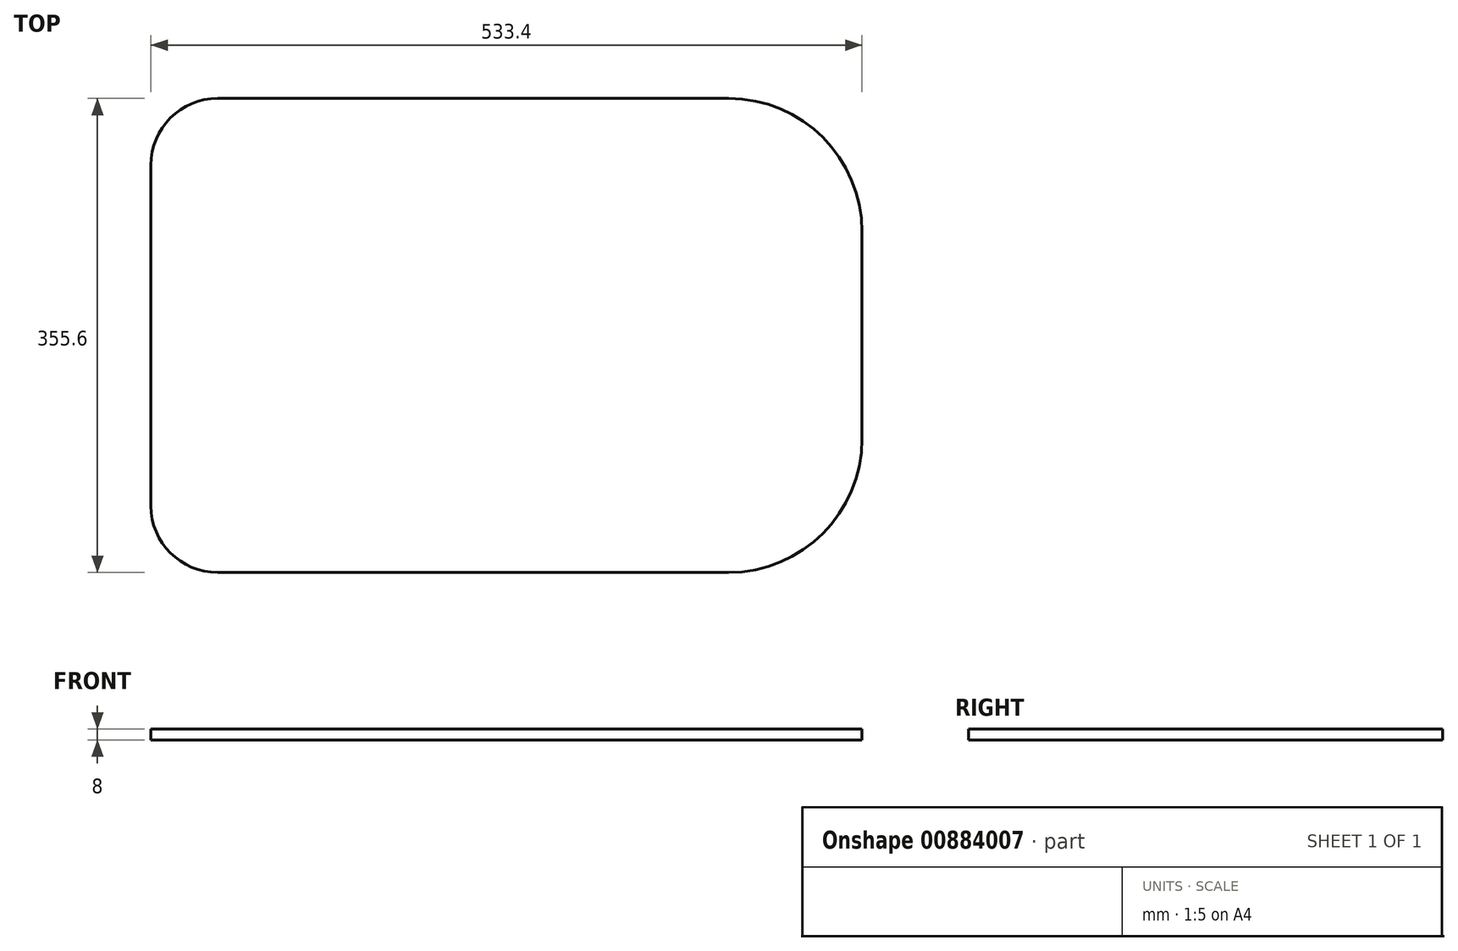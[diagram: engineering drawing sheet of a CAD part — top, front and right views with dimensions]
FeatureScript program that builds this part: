
annotation { "Feature Type Name" : "Feature", "Feature Type Description" : "" }
export const myFeature = defineFeature(function(context is Context, id is Id, definition is map)
    precondition{}
    {
        {
            var Q0;
            Q0=qCreatedBy(makeId("Top.planeOp"),FACE);
            var sketch = newSketch(context, id + "F0", { "sketchPlane" : qUnion([Q0])});
            skLineSegment(sketch, "E0.bottom", {"start": v(266.7, 177.8) * mm, "end": v(-266.7, 177.8) * mm});
            skLineSegment(sketch, "E0.top", {"start": v(266.7, -177.8) * mm, "end": v(-266.7, -177.8) * mm});
            skLineSegment(sketch, "E0.left", {"start": v(266.7, 177.8) * mm, "end": v(266.7, -177.8) * mm});
            skLineSegment(sketch, "E0.right", {"start": v(-266.7, 177.8) * mm, "end": v(-266.7, -177.8) * mm});
            skPoint(sketch, "E0.middle", {"position": v(0, 0) * mm});
            skSolve(sketch);
        }
        {
            var Q0;
            Q0=makeQuery(id+"F0.imprint","IMPRINT",FACE,{"disambiguationData":[TD([[makeQuery(id+"F0.imprint","IMPRINT",EDGE,{"derivedFrom":sQuery(id+"F0.wireOp",EDGE,"E0.bottom")}),1.0]])]});
            extrude(context, id + "F1", {"entities" : qUnion([Q0]), "depth" : 8 * mm, "offsetDistance" : 25.4 * mm});
        }
        {
            var Q0;
            Q0=makeQuery(id+"F1.opExtrude","SWEPT_EDGE",EDGE,{"disambiguationData":[OSD([sQuery(id+"F0.wireOp",EDGE,"E0.bottom"),sQuery(id+"F0.wireOp",EDGE,"E0.left")])]});
            var Q1;
            Q1=makeQuery(id+"F1.opExtrude","SWEPT_EDGE",EDGE,{"disambiguationData":[OSD([sQuery(id+"F0.wireOp",EDGE,"E0.top"),sQuery(id+"F0.wireOp",EDGE,"E0.left")])]});
            fillet(context, id + "F2", {"entities" : qUnion([Q0, Q1]), "radius" : 100 * mm, "tangentPropagation" : true, "allowEdgeOverflow" : false});
        }
        {
            var Q0;
            Q0=makeQuery(id+"F1.opExtrude","SWEPT_EDGE",EDGE,{"disambiguationData":[OSD([sQuery(id+"F0.wireOp",EDGE,"E0.top"),sQuery(id+"F0.wireOp",EDGE,"E0.right")])]});
            var Q1;
            Q1=makeQuery(id+"F1.opExtrude","SWEPT_EDGE",EDGE,{"disambiguationData":[OSD([sQuery(id+"F0.wireOp",EDGE,"E0.bottom"),sQuery(id+"F0.wireOp",EDGE,"E0.right")])]});
            fillet(context, id + "F3", {"entities" : qUnion([Q0, Q1]), "radius" : 50 * mm, "tangentPropagation" : true, "allowEdgeOverflow" : false});
        }
    });
